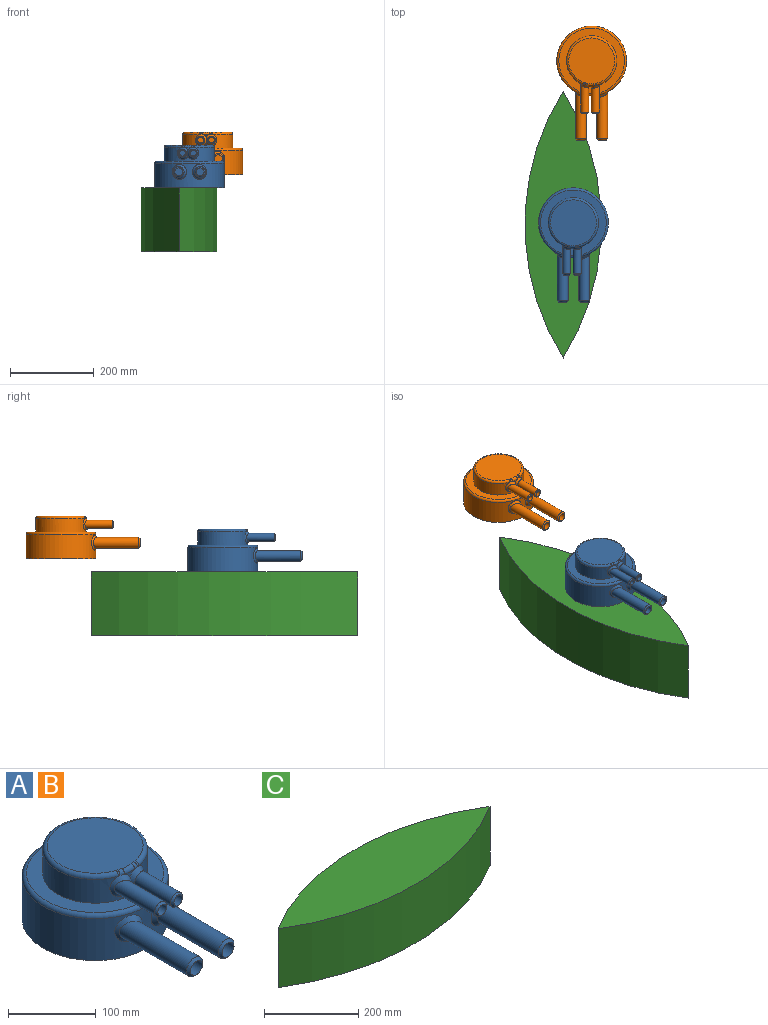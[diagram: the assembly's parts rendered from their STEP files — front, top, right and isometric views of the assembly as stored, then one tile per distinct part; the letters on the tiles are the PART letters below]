
ASSEMBLY  parts=3 mates=1
PART A: 33 faces, bbox 180.6x279.1x102.1 mm
  f0: cylinder r=59.69mm len=15.55mm, axis (0,0,-1), area 52.8mm2, adj f22,f23,f29
  f1: cylinder r=59.69mm len=119.38mm, axis (0,0,-1), area 11113mm2, adj f3,f22,f23,f28
  f2: cylinder r=83.17mm len=166.35mm, axis (0,0,-1), area 28557.3mm2, adj f4,f18,f20,f32
  f3: plane 156.19x156.19mm, normal (0,0,1), area 7966.4mm2, adj f1,f32
  f4: plane 166.35x166.35mm, normal (0,0,-1), area 21733.3mm2, adj f2
  f5: cylinder r=12.7mm len=101.38mm, axis (0,1,0), area 8089.9mm2, adj f20,f21
  f6: cylinder r=12.7mm len=101.38mm, axis (0,1,0), area 8089.9mm2, adj f18,f19
  f7: cylinder r=9.53mm len=201.3mm, axis (0,-1,0), area 12047mm2, adj f8,f19
  f8: plane 19.05x19.05mm, normal (0,-1,0), area 285mm2, adj f7
  f9: cylinder r=9.53mm len=201.3mm, axis (0,-1,0), area 12047mm2, adj f10,f21
  f10: plane 19.05x19.05mm, normal (0,-1,0), area 285mm2, adj f9
  f11: plane 109.74x109.74mm, normal (0,0,1), area 9369.3mm2, adj f26,f27,f28,f29,f30,f31
  f12: cylinder r=9.53mm len=65.11mm, axis (0,1,0), area 3603.8mm2, adj f22,f25
  f13: cylinder r=9.53mm len=61.56mm, axis (0,1,0), area 3507.4mm2, adj f23,f24
  f14: cylinder r=6.99mm len=99.38mm, axis (0,-1,0), area 4347.4mm2, adj f15,f24
  f15: plane 13.97x13.97mm, normal (0,-1,0), area 153.3mm2, adj f14
  f16: cylinder r=6.99mm len=99.06mm, axis (0,-1,0), area 4347.6mm2, adj f17,f25
  f17: plane 13.97x13.97mm, normal (0,-1,0), area 153.3mm2, adj f16
  f18: bspline ~35.54x33.5mm, area 657.4mm2, adj f2,f6
  f19: cone r=7.62mm half-angle=45deg, axis (0,1,0), area 313.5mm2, adj f6,f7
  f20: bspline ~35.54x33.49mm, area 657.4mm2, adj f2,f5
  f21: cone r=7.62mm half-angle=45deg, axis (0,1,0), area 313.5mm2, adj f5,f9
  f22: bspline ~29.17x26.9mm, area 488mm2, adj f0,f1,f12,f23,f26,f27
  f23: bspline ~29.21x26.89mm, area 479.9mm2, adj f0,f1,f13,f22,f30,f31
  f24: cone r=4.45mm half-angle=45deg, axis (0,1,0), area 186.3mm2, adj f13,f14
  f25: cone r=4.45mm half-angle=45deg, axis (0,1,0), area 186.3mm2, adj f12,f16
  f26: bspline ~6.13x5.63mm, area 16.1mm2, adj f11,f22,f27,f28
  f27: bspline ~8.4x6.88mm, area 43.4mm2, adj f11,f22,f26,f29
  f28: torus R=54.61mm, axis (0,0,1), area 2655mm2, adj f1,f11,f26,f30
  f29: torus R=54.61mm, axis (0,0,1), area 120.8mm2, adj f0,f11,f27,f31
  f30: bspline ~5.84x5.52mm, area 21.7mm2, adj f11,f23,f28,f31
  f31: bspline ~7.7x6.13mm, area 36.3mm2, adj f11,f23,f29,f30
  f32: torus R=78.09mm, axis (0,0,1), area 4077.6mm2, adj f2,f3
PART B: same geometry as A
PART C: 4 faces, bbox 635x182.1x152.4 mm
  f0: cylinder r=599.06mm len=635mm, axis (0,0,-1), area 101996.2mm2, adj f1,f2,f3
  f1: cylinder r=599.06mm len=635mm, axis (0,0,-1), area 101996.2mm2, adj f0,f2,f3
  f2: plane 635x182.12mm, normal (0,0,1), area 78349.4mm2, adj f0,f1
  f3: plane 635x182.12mm, normal (0,0,-1), area 78349.4mm2, adj f0,f1
PLACE A t=(-96.87,7.39,190.59)mm
PLACE B t=(-53.45,392.85,221.9)mm
PLACE C rot(axis=(0,0,1),90deg) t=(-121.29,3.3,38.19)mm
MATE planar C.f2 <-> A.f2  axis (0,0,1) through (-121.29,3.3,190.59)mm
